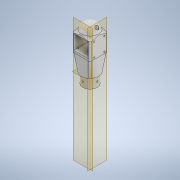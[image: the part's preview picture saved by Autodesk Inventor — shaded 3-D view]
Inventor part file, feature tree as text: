
AUTODESK INVENTOR PART (.ipt)
format: ipt  version: 2022.3 (Build 263350000, 350)  size: 615,424 bytes
history: native  units: mm
features: sketch x18, extrude x12, hole x5, thicken_offset x5, plane x4, fillet x3, revolve x2, mirror x2, loft x1, other x1, projected_geometry x1
ambient origin geometry x8: Origin, YZ Plane, XZ Plane, XY Plane, X Axis, Y Axis, Z Axis, Center Point
bodies: Solid1 (feature_tree)
feature tree (54):
  extrude  "Extrusion1"  Depth=4.0mm
  revolve  "Revolution1"  [1 undecoded]
  plane  "Work Plane1"
  extrude  "Extrusion2"  Depth=100.0mm
  extrude  "Extrusion3"  Depth=150.0mm
  plane  "Work Plane2"
  sketch  "Sketch5"  dims[d12=100.0mm d13=90.0deg]
  fillet  "Fillet1"  Radius=4.0mm
  loft  "Loft1"
  extrude  "Extrusion4"  Depth=5.0mm
  sketch  "Sketch11"  dims[d16=65.0mm d17=65.0mm]
  extrude  "Extrusion7"  Depth=65.0mm
  extrude  "Extrusion8"  Depth=15.0mm
  extrude  "Extrusion9"  Depth=10.0mm TaperAngle=0.0deg
  hole  "Hole2"  [1 undecoded]
  extrude  "Extrusion10"  Depth=50.0mm
  revolve  "Revolution2"  Angle=90.0deg
  fillet  "Fillet3"  [1 undecoded]
  hole  "Hole3"  [1 undecoded]
  hole  "Hole4"  [1 undecoded]
  extrude  "Extrusion14"  Depth=45.0mm
  sketch  "Sketch22"  dims[d58=45.0mm d59=0.0mm d60=45.0mm]
  extrude  "Extrusion15"  Depth=42.0mm TaperAngle=0.0deg
  extrude  "Extrusion16"  Depth=31.0mm
  plane  "Work Plane3"
  plane  "Work Plane4"
  sketch  "Sketch23"  dims[d61=22.0mm d62=42.0mm d63=0.0mm]
  sketch  "Sketch24"  dims[d64=31.0mm d65=31.0mm]
  hole  "Hole5"  [1 undecoded]
  hole  "Hole6"  [1 undecoded]
  mirror  "Mirror1"
  mirror  "Mirror2"
  thicken_offset  "Thicken1"
  thicken_offset  "Thicken2"
  thicken_offset  "Thicken3"
  thicken_offset  "Thicken4"
  thicken_offset  "Thicken5"
  extrude  "Extrusion17"  Depth=26.0mm
  fillet  "Fillet4"  [1 undecoded]
  sketch  "Sketch1"  dims[d0=80.0mm d1=4.0mm]
  sketch  "Sketch2"  dims[d2=40.0mm d3=0.0mm d4=88.0mm]
  sketch  "Sketch3"  dims[d5=50.0mm d8=100.0mm]
  sketch  "Sketch4"  dims[d9=25.0mm d10=150.0mm d11=4.0mm]
  other  "Edges1"
  sketch  "Sketch7"  dims[d14=-52.5mm d15=5.0mm]
  projected_geometry  "Projected Loop2"
  sketch  "Sketch12"  dims[d18=5.0mm d19=15.0mm]
  sketch  "Sketch13"  dims[d20=10.0mm d21=5.0mm d22=0.0mm]
  sketch  "Sketch14"  dims[d23=52.0mm d24=52.0mm]
  sketch  "Sketch15"  dims[d25=5.0mm d26=0.0mm d27=50.0mm]
  sketch  "Sketch16"  dims[d28=5.0mm d29=0.0mm d30=90.0deg d31=0.0mm d32=90.0deg]
  sketch  "Sketch17"  dims[d33=100.0mm d34=0.0mm d54=5.0mm]
  sketch  "Sketch21"  dims[d55=4.5mm d56=5.0mm d57=0.0mm]
  sketch  "Sketch25"  dims[d66=3.4mm d67=6.0mm d68=5.9mm d69=2.0mm d70=90.0deg d71=5.0mm d72=0.0mm d73=3.0mm d74=0.0mm d75=26.0mm d76=26.0mm d77=90.0deg d78=10.0mm d79=0.0mm d80=5.0mm d81=5.0mm d82=5.0mm d83=5.068mm d84=3.4mm d85=6.0mm d86=4.1mm d87=5.1mm d88=90.0deg d89=2.2mm d90=0.0mm d91=5.0mm d92=5.0mm d93=5.0mm d94=5.068mm d95=3.4mm d96=6.0mm d97=4.1mm d98=5.1mm d99=90.0deg d100=2.2mm d101=0.0mm d102=30.0mm d103=40.0mm d104=30.0mm d105=40.0mm d143=10.0mm d144=0.0mm d145=30.0mm d146=10.0mm d147=0.0mm d148=30.0mm d149=0.0mm d150=21.0mm d151=21.0mm d152=3.4mm d153=6.0mm d154=4.1mm d155=5.1mm d156=90.0deg d157=1.2mm d158=0.0mm d159=3.4mm d160=6.0mm d161=4.1mm d162=5.1mm d163=90.0deg d164=1.2mm d165=0.0mm d166=42.0mm d167=0.5mm d168=0.5mm d169=0.5mm d170=0.5mm d171=1.0mm d172=1.0mm d173=1.0mm d174=1.0mm d175=1.0mm d176=1.0mm d177=10.0mm d178=10.0mm d179=12.0mm d180=12.0mm d181=7.0mm d182=2.0mm d183=2.5mm d184=2.5mm d185=0.0mm d186=0.0mm d187=2.0mm d125=0.872665mm d126=0.872665mm d131=1.0mm d132=1.0mm d133=1.0mm d134=0.15mm d135=0.25mm d136=0.375mm d137=14.3117mm d138=0.75mm d139=20.594885mm d140=0.0625mm d141=0.75mm d142=0.375mm]
note: 8 required parameter values undecoded (feature->parameter linkage not recoverable at this tier; creation-order binding heuristic only, values carry confidence <= 0.55)